# Revit family: Access_Door-Acudor-Universal_Flush-ED-2002_Series
name_source: partatom
category: Specialty Equipment
revit_build: Autodesk Revit 2014 (Build: 20130308_1515(x64)
units: mm (PartAtom-declared; Revit-internal decimal feet)

## types (10) — shared parameters
Allen Head Cam Latch = No
Assembly Code = C1020700
Cylinder Lock = Yes
Default Elevation = 48"
Description = Universal Flush
Finish = Steel-Acudor-18 Gauge-Alkyd White Enamel
Installation Type = Wall Mounted
Length = 1 7/16"
Manufacturer = Acudor
Material = Steel-Acudor-18 Gauge-Alkyd White Enamel
Product Documentation Link = https://www.acudor.com
Product Page URL = https://www.acudor.com
Screwdriver Operated Cam Latch = Yes
Spanner Head Cam Latch = No
URL = http://acudor.com

## per-type parameters (varying)
| type | Height | Latch 1 | Latch 2 | Latch 2 Height | Latch Height | Width |
| ED-2002 8x8 | 8" | Yes | No | 1/4" | 1" | 8" |
| ED-2002 12x12 | 12" | Yes | No | 1/4" | 1" | 12" |
| ED-2002 16x16 | 16" | Yes | No | 1/4" | 1" | 16" |
| ED-2002 18x18 | 18" | Yes | No | 1/4" | 1" | 18" |
| ED-2002 24x24 | 24" | Yes | No | 1/4" | 1" | 24" |
| ED-2002 24x36 | 36" | No | Yes | 1" | 1/4" | 24" |
| ED-2002 6x6 | 6" | Yes | No | 1/4" | 1" | 6" |
| ED-2002 10x10 | 10" | Yes | No | 1/4" | 1" | 10" |
| ED-2002 14x14 | 14" | Yes | No | 1/4" | 1" | 14" |
| ED-2002 20x20 | 20" | Yes | No | 1/4" | 1" | 20" |

note: column(s) folded — value = type name in every type: Model

## geometry (parser evidence)
native form markers: Sweep x1
no freeform markers — native parametric forms only
